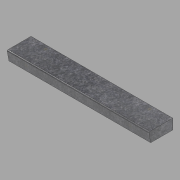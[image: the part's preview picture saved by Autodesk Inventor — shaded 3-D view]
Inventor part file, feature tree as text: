
AUTODESK INVENTOR PART (.ipt)
format: ipt  version: 2022.1 (Build 261234020, 234B)  size: 113,152 bytes
history: native  units: in
note: dims shown in document units (in); Inventor stores cm internally (conversion verified against a paired STEP export)
features: other x3, extrude x1, sketch x1
ambient origin geometry x8: Origin, YZ Plane, XZ Plane, XY Plane, X Axis, Y Axis, Z Axis, Center Point
bodies: Solid1 (feature_tree)
feature tree (5):
  other  "Blocks"
  extrude  "Extrusion1"  Depth=83.375in TaperAngle=0.0deg
  sketch  "Sketch1"  dims[d0=13.0in d1=6.0in d2=13.5in d3=0.5in d4=0.5in d5=83.375in d6=0.0in]
  other  "Profile"
  other  "Profile:1"
